# Revit family: NLRS_33_GM_FB_TC_STORAX_vloerluik_BVE_BCB
name_source: partatom
category: Generic Models
revit_build: Autodesk Revit 2014 (Build: 20130308_1515(x64)
units: mm (PartAtom-declared; Revit-internal decimal feet)

## types (11) — shared parameters
Default Elevation = 1219 mm
Manufacturer = Storax
Model = BV
URL = http://www.storax.nl
belasting = 125 kN
binnenluik = tbv betonvulling
brandwerend 90 min = nee
gasdrukveer = nee
geïsoleerd = nee
materiaal = bcb_staal
productgroep = Vloerluiken
rubberen_afdichting = enkel
scharnierend = nee
sluiting = 4
vergrendeling = nee
vullen_met_beton = ja

## per-type parameters (varying)
| type | binnenmaat_breedte | binnenmaat_lengte | gewicht | uitwendige_breedte | uitwendige_lengte |
| BVE 33 | 300 mm  [stored 0.984252 ft] | 300 mm  [stored 0.984252 ft] | 10 | 435 mm  [stored 1.42717 ft] | 435 mm  [stored 1.42717 ft] |
| BVE 45 | 450 mm | 450 mm | 16 | 585 mm | 585 mm |
| BVE 55 | 550 mm | 550 mm | 17 | 685 mm | 685 mm |
| BVE 64 | 600 mm | 400 mm  [stored 1.31234 ft] | 17 | 735 mm | 535 mm  [stored 1.75525 ft] |
| BVE 66 | 600 mm | 600 mm | 21 | 735 mm | 735 mm |
| BVE 86 | 800 mm  [stored 2.62467 ft] | 600 mm | 27 | 935 mm | 735 mm |
| BVE 88 | 800 mm  [stored 2.62467 ft] | 800 mm  [stored 2.62467 ft] | 31 | 935 mm | 935 mm |
| BVE 106 | 1000 mm  [stored 3.28084 ft] | 600 mm | 31 | 1135 mm  [stored 3.72375 ft] | 735 mm |
| BVE 108 | 1000 mm  [stored 3.28084 ft] | 800 mm  [stored 2.62467 ft] | 37 | 1135 mm  [stored 3.72375 ft] | 935 mm |
| BVE 110 | 1000 mm  [stored 3.28084 ft] | 1000 mm  [stored 3.28084 ft] | 42 | 1135 mm  [stored 3.72375 ft] | 1135 mm  [stored 3.72375 ft] |
| maatwerk | 300 mm  [stored 0.984252 ft] | 300 mm  [stored 0.984252 ft] | 10 | 435 mm  [stored 1.42717 ft] | 435 mm  [stored 1.42717 ft] |

note: [stored X ft] marks values corroborated as IEEE doubles in the binary element streams (Revit-internal decimal feet)

## geometry (parser evidence)
native form markers: Blend x803, Sweep x8
no freeform markers — native parametric forms only
